# Revit family: ITK Термостат аналоговый
name_source: partatom
category: Электрооборудование
revit_build: Autodesk Revit 2016 (Build: 20160314_0715(x64)
units: mm (PartAtom-declared; Revit-internal decimal feet)

## family parameters
Всегда вертикально = Да
На основе рабочей плоскости = Нет
Общий = Нет
При загрузке вырезать с полостями = Нет
Размер круглого соединителя = Использовать диаметр
Тип детали = Другая панель
Точка расчета площади = Нет

## types (1)
- TS-A1
    ADSK_Единица измерения = шт
    ADSK_Завод-изготовитель = IEK
    ADSK_Классификация нагрузок = Прочее
    ADSK_Количество фаз = 1
    ADSK_Количество фаз числовое = 1
    ADSK_Коэффициент мощности = 1
    ADSK_Марка = TS-A1
    ADSK_Масса = 0
    ADSK_Наименование = ITK Термостат аналоговый, серый
    ADSK_Наименование краткое = TS-A1
    ADSK_Напряжение = 220 В
    ADSK_Номинальная мощность = 0 Вт
    ADSK_Полная мощность = 0 В·А
    ADSK_Ток = 0 А
    URL = http://www.itk-group.ru
    Высота = 36 мм
    Глубина = 44 мм
    Изготовитель = ITK
    Материал = Окраска - RAL 7035
    Описание = Термостат аналоговый применяется для организации управления работы вентиляторных потолочных панелей в зависимости от требуемой температуры включения/отключения. Термостат необходим в том случае, если панель данным термостатом не скомплектована.

Тип термостата: механический замыкающий нормально разомкнутый (NO). 
Номинальное рабочее напряжение: 230В. Частота тока: 50Гц.
Диапазон регулировки температуры: от 0 до +60 °С.
Разность температур переключения: 9-11 °С.
Срок службы, циклов В-О: более 100 000.

Для установки термостата внутри шкафа на вертикальные монтажные профили термостат комплектуется монтажным уголком. Размер термостата без уголка: 60х33х43 мм. Размер с уголком: 60х70х43 мм.
Комплект поставки: термостат, монтажный уголок, комплект крепления винт-шайба-гайка.
Совместимы со всеми 19-дюймовыми шкафами и стойками ITK.
Обладают современным привлекательным дизайном и продуманной конструкцией.
Удобны в монтаже и эксплуатации.
Соответствие международным стандартам ISO9001, IEC 297, ISO/IEC 11801. 
Сертифицированы по ГОСТ Р.
Все аксессуары идут с крепежом.
Возможно исполнение в двух цветах: серый (RAL7035) и черный (RAL9005).
Всегда в наличии на складе.
Гарантия на все аксессуары до 2-х лет.
    Совместимость = Linea N, S, F, W, O
    Ширина = 44 мм
